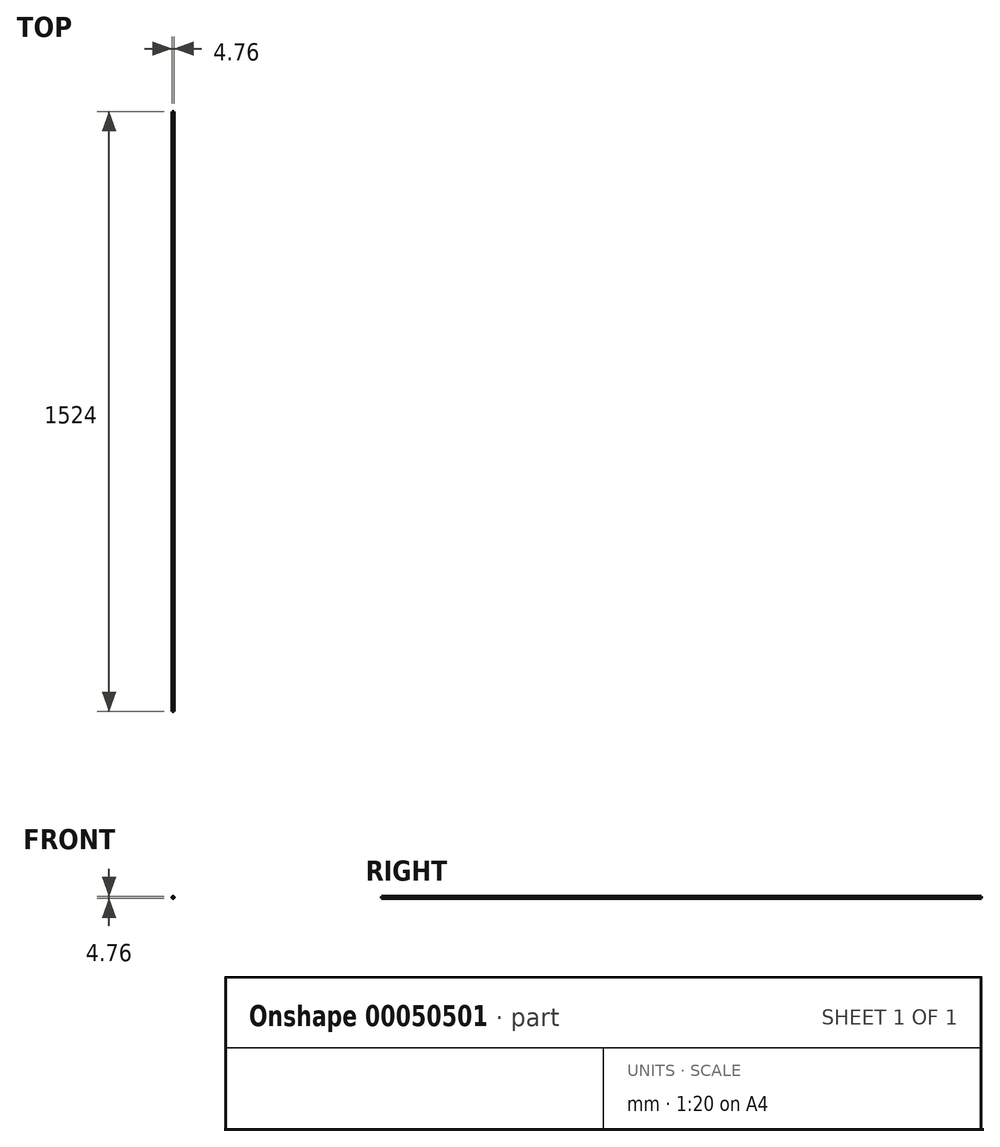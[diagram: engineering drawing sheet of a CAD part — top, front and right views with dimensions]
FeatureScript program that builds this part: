
annotation { "Feature Type Name" : "Feature", "Feature Type Description" : "" }
export const myFeature = defineFeature(function(context is Context, id is Id, definition is map)
    precondition{}
    {
        {
            var Q0;
            Q0=qCreatedBy(makeId("Front.planeOp"),FACE);
            var sketch = newSketch(context, id + "F0", { "sketchPlane" : qUnion([Q0])});
            skCircle(sketch, "E0", {"center": v(0, 0) * mm, "radius": 2.38 * mm});
            skSolve(sketch);
        }
        {
            var Q0;
            Q0 = qSketchRegion(id + "F0", true);
            extrude(context, id + "F1", {"entities" : qUnion([Q0]), "endBound" : BoundingType.SYMMETRIC, "depth" : 1524 * mm});
        }
    });
